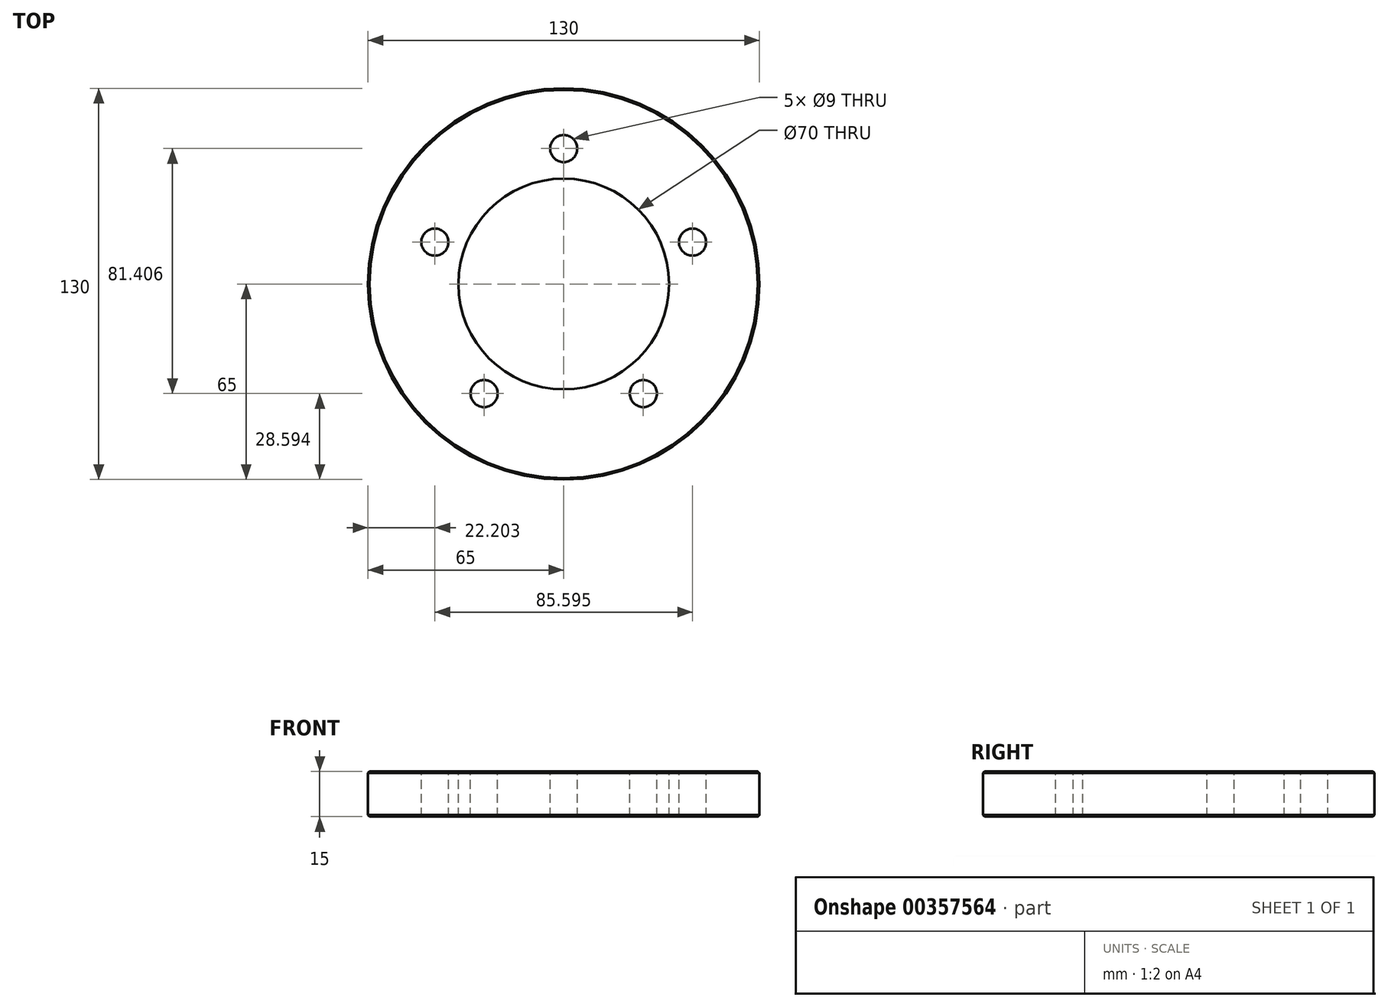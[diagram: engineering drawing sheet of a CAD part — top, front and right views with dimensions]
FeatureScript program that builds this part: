
annotation { "Feature Type Name" : "Feature", "Feature Type Description" : "" }
export const myFeature = defineFeature(function(context is Context, id is Id, definition is map)
    precondition{}
    {
        {
            var Q0;
            Q0=qCreatedBy(makeId("Top.planeOp"),FACE);
            var sketch = newSketch(context, id + "F0", { "sketchPlane" : qUnion([Q0])});
            skCircle(sketch, "E0", {"center": v(0, 0) * mm, "radius": 65 * mm});
            skSolve(sketch);
        }
        {
            var Q0;
            Q0 = qSketchRegion(id + "F0", true);
            extrude(context, id + "F1", {"entities" : qUnion([Q0]), "depth" : 15 * mm});
        }
        {
            var Q0;
            Q0=makeQuery(id+"F1.opExtrude","CAP_FACE",FACE,{"disambiguationData":[OSD([sQuery(id+"F0.wireOp",EDGE,"E0")])],"isStart":false});
            var sketch = newSketch(context, id + "F2", { "sketchPlane" : qUnion([Q0])});
            skCircle(sketch, "E1", {"center": v(0, 0) * mm, "radius": 45 * mm});
            skCircle(sketch, "E2", {"center": v(0, 45) * mm, "radius": 4.5 * mm});
            skCircle(sketch, "E3.1.0", {"center": v(-42.8, 13.9) * mm, "radius": 4.5 * mm});
            skCircle(sketch, "E3.2.0", {"center": v(-26.45, -36.4) * mm, "radius": 4.5 * mm});
            skCircle(sketch, "E3.3.0", {"center": v(26.45, -36.4) * mm, "radius": 4.5 * mm});
            skCircle(sketch, "E3.4.0", {"center": v(42.8, 13.9) * mm, "radius": 4.5 * mm});
            skSolve(sketch);
        }
        {
            var Q0;
            {var subQ0=sQuery(id+"F2.wireOp",EDGE,"E3.1.0");var subQ1=sQuery(id+"F2.wireOp",EDGE,"E1");var subQ2=makeQuery(id+"F2.imprint","INTERSECT",VERTEX,{"disambiguationData":[OD(0.0)],"derivedFrom":[subQ1,subQ0]});Q0=makeQuery(id+"F2.imprint","IMPRINT",FACE,{"disambiguationData":[TD([[makeQuery(id+"F2.imprint","IMPRINT",EDGE,{"disambiguationData":[TD([[subQ2,-1.0]])],"derivedFrom":subQ1}),1.0]])]});}
            var Q1;
            {var subQ0=sQuery(id+"F2.wireOp",EDGE,"E3.1.0");var subQ1=sQuery(id+"F2.wireOp",EDGE,"E1");var subQ2=makeQuery(id+"F2.imprint","INTERSECT",VERTEX,{"disambiguationData":[OD(0.0)],"derivedFrom":[subQ1,subQ0]});Q1=makeQuery(id+"F2.imprint","IMPRINT",FACE,{"disambiguationData":[TD([[makeQuery(id+"F2.imprint","IMPRINT",EDGE,{"disambiguationData":[TD([[subQ2,-1.0]])],"derivedFrom":subQ1}),-1.0]])]});}
            var Q2;
            {var subQ0=sQuery(id+"F2.wireOp",EDGE,"E2");var subQ1=sQuery(id+"F2.wireOp",EDGE,"E1");var subQ2=makeQuery(id+"F2.imprint","INTERSECT",VERTEX,{"disambiguationData":[OD(0.0)],"derivedFrom":[subQ1,subQ0]});Q2=makeQuery(id+"F2.imprint","IMPRINT",FACE,{"disambiguationData":[TD([[makeQuery(id+"F2.imprint","IMPRINT",EDGE,{"disambiguationData":[TD([[subQ2,-1.0]])],"derivedFrom":subQ1}),1.0]])]});}
            var Q3;
            {var subQ0=sQuery(id+"F2.wireOp",EDGE,"E2");var subQ1=sQuery(id+"F2.wireOp",EDGE,"E1");var subQ2=makeQuery(id+"F2.imprint","INTERSECT",VERTEX,{"disambiguationData":[OD(0.0)],"derivedFrom":[subQ1,subQ0]});Q3=makeQuery(id+"F2.imprint","IMPRINT",FACE,{"disambiguationData":[TD([[makeQuery(id+"F2.imprint","IMPRINT",EDGE,{"disambiguationData":[TD([[subQ2,-1.0]])],"derivedFrom":subQ1}),-1.0]])]});}
            var Q4;
            {var subQ0=sQuery(id+"F2.wireOp",EDGE,"E3.4.0");var subQ1=sQuery(id+"F2.wireOp",EDGE,"E1");var subQ2=makeQuery(id+"F2.imprint","INTERSECT",VERTEX,{"disambiguationData":[OD(0.0)],"derivedFrom":[subQ1,subQ0]});Q4=makeQuery(id+"F2.imprint","IMPRINT",FACE,{"disambiguationData":[TD([[makeQuery(id+"F2.imprint","IMPRINT",EDGE,{"disambiguationData":[TD([[subQ2,1.0]])],"derivedFrom":subQ1}),1.0]])]});}
            var Q5;
            {var subQ0=sQuery(id+"F2.wireOp",EDGE,"E3.4.0");var subQ1=sQuery(id+"F2.wireOp",EDGE,"E1");var subQ2=makeQuery(id+"F2.imprint","INTERSECT",VERTEX,{"disambiguationData":[OD(0.0)],"derivedFrom":[subQ1,subQ0]});Q5=makeQuery(id+"F2.imprint","IMPRINT",FACE,{"disambiguationData":[TD([[makeQuery(id+"F2.imprint","IMPRINT",EDGE,{"disambiguationData":[TD([[subQ2,1.0]])],"derivedFrom":subQ1}),-1.0]])]});}
            var Q6;
            {var subQ0=sQuery(id+"F2.wireOp",EDGE,"E3.3.0");var subQ1=sQuery(id+"F2.wireOp",EDGE,"E1");var subQ2=makeQuery(id+"F2.imprint","INTERSECT",VERTEX,{"disambiguationData":[OD(0.0)],"derivedFrom":[subQ1,subQ0]});Q6=makeQuery(id+"F2.imprint","IMPRINT",FACE,{"disambiguationData":[TD([[makeQuery(id+"F2.imprint","IMPRINT",EDGE,{"disambiguationData":[TD([[subQ2,-1.0]])],"derivedFrom":subQ1}),-1.0]])]});}
            var Q7;
            {var subQ0=sQuery(id+"F2.wireOp",EDGE,"E3.3.0");var subQ1=sQuery(id+"F2.wireOp",EDGE,"E1");var subQ2=makeQuery(id+"F2.imprint","INTERSECT",VERTEX,{"disambiguationData":[OD(0.0)],"derivedFrom":[subQ1,subQ0]});Q7=makeQuery(id+"F2.imprint","IMPRINT",FACE,{"disambiguationData":[TD([[makeQuery(id+"F2.imprint","IMPRINT",EDGE,{"disambiguationData":[TD([[subQ2,-1.0]])],"derivedFrom":subQ1}),1.0]])]});}
            var Q8;
            {var subQ0=sQuery(id+"F2.wireOp",EDGE,"E3.2.0");var subQ1=sQuery(id+"F2.wireOp",EDGE,"E1");var subQ2=makeQuery(id+"F2.imprint","INTERSECT",VERTEX,{"disambiguationData":[OD(0.0)],"derivedFrom":[subQ1,subQ0]});Q8=makeQuery(id+"F2.imprint","IMPRINT",FACE,{"disambiguationData":[TD([[makeQuery(id+"F2.imprint","IMPRINT",EDGE,{"disambiguationData":[TD([[subQ2,-1.0]])],"derivedFrom":subQ1}),-1.0]])]});}
            var Q9;
            {var subQ0=sQuery(id+"F2.wireOp",EDGE,"E3.2.0");var subQ1=sQuery(id+"F2.wireOp",EDGE,"E1");var subQ2=makeQuery(id+"F2.imprint","INTERSECT",VERTEX,{"disambiguationData":[OD(0.0)],"derivedFrom":[subQ1,subQ0]});Q9=makeQuery(id+"F2.imprint","IMPRINT",FACE,{"disambiguationData":[TD([[makeQuery(id+"F2.imprint","IMPRINT",EDGE,{"disambiguationData":[TD([[subQ2,-1.0]])],"derivedFrom":subQ1}),1.0]])]});}
            extrude(context, id + "F3", {"entities" : qUnion([Q0, Q1, Q2, Q3, Q4, Q5, Q6, Q7, Q8, Q9]), "operationType" : NewBodyOperationType.REMOVE, "endBound" : BoundingType.THROUGH_ALL, "oppositeDirection" : true, "depth" : 25 * mm});
        }
        {
            var Q0;
            Q0=makeQuery(id+"F1.opExtrude","CAP_FACE",FACE,{"disambiguationData":[OSD([sQuery(id+"F0.wireOp",EDGE,"E0")])],"isStart":false});
            var sketch = newSketch(context, id + "F4", { "sketchPlane" : qUnion([Q0])});
            skCircle(sketch, "E4", {"center": v(0, 0) * mm, "radius": 35 * mm});
            skSolve(sketch);
        }
        {
            var Q0;
            Q0=makeQuery(id+"F4.imprint","IMPRINT",FACE,{"disambiguationData":[TD([[makeQuery(id+"F4.imprint","IMPRINT",EDGE,{"derivedFrom":sQuery(id+"F4.wireOp",EDGE,"E4")}),1.0]])]});
            extrude(context, id + "F5", {"entities" : qUnion([Q0]), "operationType" : NewBodyOperationType.REMOVE, "endBound" : BoundingType.THROUGH_ALL, "oppositeDirection" : true, "depth" : 25 * mm});
        }
        {
            var Q0;
            Q0=makeQuery(id+"F1.opExtrude","CAP_EDGE",EDGE,{"disambiguationData":[OSD([sQuery(id+"F0.wireOp",EDGE,"E0")])],"isStart":false});
            chamfer(context, id + "F6", {"entities" : qUnion([Q0]), "chamferType" : ChamferType.OFFSET_ANGLE, "width" : 0.5 * mm, "oppositeDirection" : false, "angle" : 45 * degree, "tangentPropagation" : true});
        }
        {
            var Q0;
            Q0=makeQuery(id+"F1.opExtrude","CAP_EDGE",EDGE,{"disambiguationData":[OSD([sQuery(id+"F0.wireOp",EDGE,"E0")])],"isStart":true});
            chamfer(context, id + "F7", {"entities" : qUnion([Q0]), "chamferType" : ChamferType.OFFSET_ANGLE, "width" : 0.5 * mm, "oppositeDirection" : false, "angle" : 45 * degree, "tangentPropagation" : true});
        }
    });
